FREECAD ASSEMBLY — COMPONENT RECIPES ("wardrobe_corpus02_jan")

This assembly document has 10 components, labeled P0..P9 below (a component is one placed body or linked part). 6 of them carry a construction recipe — the FreeCAD feature program that regenerates the part from scratch, quoted from this document or its linked companion documents; the rest are supplied as boundary geometry only. No exploded tour is included for this assembly.
COMPONENT P0 — geometry summary ("hettich-level-adjustment"; no construction recipe available for this part):
  bounding box: 80.0 x 63.5 x 30.0 mm
  tessellated surface: 3,780 triangles
  volume: 65169 mm^3 (43% of its bounding box)
  symmetry: 2-fold rotationally symmetric about the z axis; mirror-symmetric across its x mid-plane, y mid-plane
COMPONENT P1 — geometry summary ("hettich-level-adjustment001"; no construction recipe available for this part):
  bounding box: 80.0 x 63.5 x 30.0 mm
  tessellated surface: 3,780 triangles
  volume: 65169 mm^3 (43% of its bounding box)
  symmetry: 2-fold rotationally symmetric about the z axis; mirror-symmetric across its x mid-plane, y mid-plane
COMPONENT P2 — geometry summary ("hettich-level-adjustment002"; no construction recipe available for this part):
  bounding box: 80.0 x 63.5 x 30.0 mm
  tessellated surface: 3,780 triangles
  volume: 65169 mm^3 (43% of its bounding box)
  symmetry: 2-fold rotationally symmetric about the z axis; mirror-symmetric across its x mid-plane, y mid-plane
COMPONENT P3 — geometry summary ("hettich-level-adjustment003"; no construction recipe available for this part):
  bounding box: 80.0 x 63.5 x 30.0 mm
  tessellated surface: 3,780 triangles
  volume: 65169 mm^3 (43% of its bounding box)
  symmetry: 2-fold rotationally symmetric about the z axis; mirror-symmetric across its x mid-plane, y mid-plane
COMPONENT P4 — recipe-attached ("wardrobe_backplate_corpus02_jan", a linked part whose construction recipe lives in a companion FreeCAD document of the same project; that document's serialized recipe follows).
Construction recipe (the companion document, serialized — sketch geometry with constraints, then the solid features built on it; lengths are millimeters unless a unit is written):

FCSTD DOCUMENT  (FreeCAD 1.0RUnknown)
Label: wardrobe_backplate_corpus02_jan
License: All rights reserved
LicenseURL: https://en.wikipedia.org/wiki/All_rights_reserved
objects: Sketcher::SketchObject×1, PartDesign::Pad×1, PartDesign::CoordinateSystem×1, PartDesign::Body×1
note: 7 computed .brp shape members not serialized (recipe doc carries the construction recipe); baked Part::Feature solids carry a one-line shape summary decoded from their .brp
EXTERNAL_REF file=../../mastersketch.FCStd obj=Spreadsheet

FEATURE [Sketcher::SketchObject] Sketch004
  ArcFitTolerance = 1e-06
  AttachmentSupport = -> [XZ_Plane006]
  FullyConstrained = true
  MakeInternals = false
  MapMode = 5
  Placement = pos=(0,0,0) rot=(1,0,0;1.5708rad)
  expr: Constraints[10] = mastersketch#Spreadsheet.corpus_width
  expr: Constraints[11] = mastersketch#Spreadsheet.corpus02_height
  sketch-geometry (5):
    g0: LineSegment StartX=-270 StartY=-390 StartZ=0 EndX=270 EndY=-390 EndZ=0
    g1: LineSegment StartX=270 StartY=-390 StartZ=0 EndX=270 EndY=390 EndZ=0
    g2: LineSegment StartX=270 StartY=390 StartZ=0 EndX=-270 EndY=390 EndZ=0
    g3: LineSegment StartX=-270 StartY=390 StartZ=0 EndX=-270 EndY=-390 EndZ=0
    g4: GeomPoint [constr] X=0 Y=0 Z=0
  constraints (12):
    c: Coincident(g0,g1)
    c: Coincident(g1,g2)
    c: Coincident(g2,g3)
    c: Coincident(g3,g0)
    c: Horizontal(g0)
    c: Horizontal(g2)
    c: Vertical(g1)
    c: Vertical(g3)
    c: Symmetric(g2,g0,g4)
    c: Coincident(g4,g-1)
    c: DistanceX(g0,g0) = 540
    c: DistanceY(g3,g3) = 780
FEATURE [PartDesign::Pad] Pad004
  Direction = (0,-1,2e-16)
  Length = 19
  Length2 = 10
  Placement = pos=(0,0,0) rot=(1,0,0;1.5708rad)
  Profile = -> Sketch004
  ReferenceAxis = -> Sketch004 [N_Axis]
  Refine = true
  Suppressed = false
  Type = 0
  expr: Length = mastersketch#Spreadsheet.corpus_backplate_thickness
FEATURE [PartDesign::CoordinateSystem] LCS_1
  AttacherType = Attacher::AttachEngine3D
  AttachmentSupport = -> [Pad004]
  MapMode = 45
  Placement = pos=(0,-19,-390) rot=(0.57735,0.57735,0.57735;2.0944rad)
FEATURE [PartDesign::Body] Body004  label="wardrobe_backplate_corpus02_jan"
  AllowCompound = false
  Group = -> [Sketch004,Pad004,LCS_1]
  Origin = -> Origin006
  Tip = -> Pad004
COMPONENT P5 — recipe-attached ("wardrobe_base_jan", a linked part whose construction recipe lives in a companion FreeCAD document of the same project; that document's serialized recipe follows).
Construction recipe (the companion document, serialized — sketch geometry with constraints, then the solid features built on it; lengths are millimeters unless a unit is written):

FCSTD DOCUMENT  (FreeCAD 1.0RUnknown)
Label: wardrobe_base_jan
License: All rights reserved
LicenseURL: https://en.wikipedia.org/wiki/All_rights_reserved
objects: PartDesign::CoordinateSystem×9, Sketcher::SketchObject×2, PartDesign::Pad×1, PartDesign::Body×1
note: 17 computed .brp shape members not serialized (recipe doc carries the construction recipe); baked Part::Feature solids carry a one-line shape summary decoded from their .brp
EXTERNAL_REF file=../../mastersketch.FCStd obj=Spreadsheet

FEATURE [Sketcher::SketchObject] Sketch
  ArcFitTolerance = 1e-06
  AttachmentSupport = -> [XY_Plane]
  FullyConstrained = true
  MakeInternals = false
  MapMode = 5
  expr: Constraints[10] = mastersketch#Spreadsheet.corpus_width
  expr: Constraints[11] = mastersketch#Spreadsheet.corpus_depth
  sketch-geometry (5):
    g0: LineSegment StartX=-270 StartY=-300 StartZ=0 EndX=270 EndY=-300 EndZ=0
    g1: LineSegment StartX=270 StartY=-300 StartZ=0 EndX=270 EndY=300 EndZ=0
    g2: LineSegment StartX=270 StartY=300 StartZ=0 EndX=-270 EndY=300 EndZ=0
    g3: LineSegment StartX=-270 StartY=300 StartZ=0 EndX=-270 EndY=-300 EndZ=0
    g4: GeomPoint [constr] X=0 Y=0 Z=0
  constraints (12):
    c: Coincident(g0,g1)
    c: Coincident(g1,g2)
    c: Coincident(g2,g3)
    c: Coincident(g3,g0)
    c: Horizontal(g0)
    c: Horizontal(g2)
    c: Vertical(g1)
    c: Vertical(g3)
    c: Symmetric(g2,g0,g4)
    c: Coincident(g4,g-1)
    c: DistanceX(g0,g0) = 540
    c: DistanceY(g3,g3) = 600
FEATURE [PartDesign::Pad] Pad
  Direction = (0,0,1)
  Length = 19
  Length2 = 10
  Profile = -> Sketch
  ReferenceAxis = -> Sketch [N_Axis]
  Refine = true
  Suppressed = false
  Type = 0
  expr: Length = mastersketch#Spreadsheet.corpus_outer_thickness
FEATURE [PartDesign::CoordinateSystem] LCS_1  label="LCS_left"
  AttacherType = Attacher::AttachEngine3D
  AttachmentSupport = -> [Pad]
  MapMode = 45
  Placement = pos=(-270,1.42e-14,19) rot=(0,0.707107,0.707107;3.14159rad)
FEATURE [PartDesign::CoordinateSystem] LCS_right  label="LCS-right"
  AttacherType = Attacher::AttachEngine3D
  AttachmentSupport = -> [Pad]
  MapMode = 45
  Placement = pos=(270,-1.42e-14,19) rot=(0,0.707107,0.707107;3.14159rad)
FEATURE [PartDesign::CoordinateSystem] LCS_center
  AttacherType = Attacher::AttachEngine3D
FEATURE [Sketcher::SketchObject] Sketch_1  label="feet_placement"
  ArcFitTolerance = 1e-06
  AttachmentSupport = -> [Pad]
  FullyConstrained = true
  MakeInternals = false
  MapMode = 5
  Placement = pos=(0,0,0) rot=(1,0,0;3.14159rad)
  expr: Constraints[10] = mastersketch#Spreadsheet.corpus_width - 100
  expr: Constraints[11] = mastersketch#Spreadsheet.corpus_depth - 140
  sketch-geometry (5):
    g0: LineSegment StartX=-220 StartY=-230 StartZ=0 EndX=220 EndY=-230 EndZ=0
    g1: LineSegment StartX=220 StartY=-230 StartZ=0 EndX=220 EndY=230 EndZ=0
    g2: LineSegment StartX=220 StartY=230 StartZ=0 EndX=-220 EndY=230 EndZ=0
    g3: LineSegment StartX=-220 StartY=230 StartZ=0 EndX=-220 EndY=-230 EndZ=0
    g4: GeomPoint [constr] X=0 Y=0 Z=0
  constraints (12):
    c: Coincident(g0,g1)
    c: Coincident(g1,g2)
    c: Coincident(g2,g3)
    c: Coincident(g3,g0)
    c: Horizontal(g0)
    c: Horizontal(g2)
    c: Vertical(g1)
    c: Vertical(g3)
    c: Symmetric(g2,g0,g4)
    c: Coincident(g4,g-1)
    c: DistanceX(g0,g0) = 440
    c: DistanceY(g3,g3) = 460
FEATURE [PartDesign::CoordinateSystem] LCS_2  label="LCS_feet0"
  AttacherType = Attacher::AttachEngine3D
  AttachmentSupport = -> [Sketch_1]
  MapMode = 1
  Placement = pos=(-220,-230,0) rot=(0,0,1;0rad)
FEATURE [PartDesign::CoordinateSystem] LCS_feet1
  AttacherType = Attacher::AttachEngine3D
  AttachmentSupport = -> [Sketch_1]
  MapMode = 1
  Placement = pos=(220,-230,0) rot=(0,0,1;0rad)
FEATURE [PartDesign::CoordinateSystem] LCS_feet2
  AttacherType = Attacher::AttachEngine3D
  AttachmentSupport = -> [Sketch_1]
  MapMode = 1
  Placement = pos=(220,230,0) rot=(0,0,1;0rad)
FEATURE [PartDesign::CoordinateSystem] LCS_feet3
  AttacherType = Attacher::AttachEngine3D
  AttachmentSupport = -> [Sketch_1]
  MapMode = 1
  Placement = pos=(-220,230,0) rot=(0,0,1;0rad)
FEATURE [PartDesign::CoordinateSystem] LCS_back
  AttacherType = Attacher::AttachEngine3D
  AttachmentSupport = -> [Pad]
  MapMode = 45
  Placement = pos=(0,300,0) rot=(0.57735,0.57735,0.57735;2.0944rad)
FEATURE [PartDesign::CoordinateSystem] LCS_door
  AttacherType = Attacher::AttachEngine3D
  AttachmentSupport = -> [Pad]
  MapMode = 7
  Placement = pos=(270,-300,0) rot=(0,1,0;3.14159rad)
FEATURE [PartDesign::Body] Body  label="wardrobe_base_jan"
  AllowCompound = false
  Group = -> [Sketch,Pad,LCS_1,LCS_right,LCS_center,Sketch_1,LCS_2,LCS_feet1,LCS_feet2,LCS_feet3,LCS_back,LCS_door]
  Origin = -> Origin
  Tip = -> Pad
COMPONENT P6 — recipe-attached ("wardrobe_door_corpus02_jan", a linked part whose construction recipe lives in a companion FreeCAD document of the same project; that document's serialized recipe follows).
Construction recipe (the companion document, serialized — sketch geometry with constraints, then the solid features built on it; lengths are millimeters unless a unit is written):

FCSTD DOCUMENT  (FreeCAD 1.0R39285 (Git))
Label: wardrobe_door_corpus02_jan
License: All rights reserved
LicenseURL: https://en.wikipedia.org/wiki/All_rights_reserved
objects: TechDraw::DrawViewDimension×5, PartDesign::CoordinateSystem×2, TechDraw::DrawProjGroupItem×2, Sketcher::SketchObject×1, PartDesign::Pad×1, PartDesign::Body×1, TechDraw::DrawSVGTemplate×1, TechDraw::DrawViewAnnotation×1, TechDraw::DrawPage×1, App::Part×1
note: 15 computed .brp shape members not serialized (recipe doc carries the construction recipe); baked Part::Feature solids carry a one-line shape summary decoded from their .brp
EXTERNAL_REF file=../../mastersheet.FCStd obj=Spreadsheet
EXTERNAL_REF file=../../mastersketch.FCStd obj=Sketch

FEATURE [Sketcher::SketchObject] Sketch
  ArcFitTolerance = 1e-06
  AttachmentSupport = -> [XY_Plane]
  FullyConstrained = true
  MakeInternals = false
  MapMode = 5
  expr: Constraints[0] = mastersketch#Sketch.Constraints.corpus02_door_height
  expr: Constraints[10] = mastersketch#Sketch.Constraints.alpha
  expr: Constraints[3] = mastersheet#Spreadsheet.corpus_width - 5
  sketch-geometry (4):
    g0: LineSegment StartX=0 StartY=0 StartZ=0 EndX=0 EndY=1413.69 EndZ=0
    g1: LineSegment StartX=0 StartY=0 StartZ=0 EndX=-535 EndY=0 EndZ=0
    g2: LineSegment StartX=-535 StartY=0 StartZ=0 EndX=-535 EndY=787.688 EndZ=0
    g3: LineSegment StartX=-535 StartY=787.688 StartZ=0 EndX=0 EndY=1413.69 EndZ=0
  constraints (11):
    c: Distance(g0) = 1413.69
    c: Coincident(g0,g-1)
    c: Vertical(g0)
    c: Distance(g1) = 535
    c: Coincident(g1,g0)
    c: PointOnObject(g1,g-1)
    c: Vertical(g2)
    c: Coincident(g3,g2)
    c: Coincident(g2,g1)
    c: Coincident(g3,g0)
    c: Angle(g2,g3) = 2.43442
FEATURE [PartDesign::Pad] Pad
  Direction = (0,0,1)
  Length = 19
  Length2 = 10
  Profile = -> Sketch
  ReferenceAxis = -> Sketch [N_Axis]
  Refine = true
  Suppressed = false
  Type = 0
FEATURE [PartDesign::Body] Body  label="wardrobe_door_corpus02_jan"
  AllowCompound = false
  Group = -> [Sketch,Pad]
  Origin = -> Origin
  Tip = -> Pad
FEATURE [PartDesign::CoordinateSystem] LCS_1
  AttacherType = Attacher::AttachEngine3D
  AttachmentSupport = -> [Pad]
  MapMode = 7
  Placement = pos=(0,0,0) rot=(1,0,0;1.5708rad)
FEATURE [TechDraw::DrawSVGTemplate] Template  label="Vorlage"
  Height = 210
  Orientation = 1
  Template = <userpath>/scoop/apps/freecad/current/data/Mod/TechDraw/Templates/A4_Landscape_TD.svg
  Width = 297
FEATURE [TechDraw::DrawProjGroupItem] View
  CoarseView = false
  Direction = (0,1e-16,-1)
  Focus = 100
  HardHidden = false
  IsoCount = 0
  IsoHidden = false
  IsoVisible = false
  LockPosition = false
  Perspective = false
  Rotation = 0
  RotationVector = (1,0,0)
  Scale = 0.1
  ScaleType = 2
  ScrubCount = 1
  SeamHidden = false
  SeamVisible = false
  SmoothHidden = false
  SmoothVisible = true
  Source = -> [Body]
  Type = 0
  X = 139.755
  XDirection = (-1e-16,-1,-1e-16)
  Y = 148.199
FEATURE [TechDraw::DrawProjGroupItem] View001
  CoarseView = false
  Direction = (-1,-1e-16,0)
  Focus = 100
  HardHidden = false
  IsoCount = 0
  IsoHidden = false
  IsoVisible = false
  LockPosition = false
  Perspective = false
  Rotation = 0
  RotationVector = (1,0,0)
  Scale = 0.1
  ScaleType = 2
  ScrubCount = 1
  SeamHidden = false
  SeamVisible = false
  SmoothHidden = false
  SmoothVisible = true
  Source = -> [Body]
  Type = 0
  X = 139.755
  XDirection = (1e-16,-1,0)
  Y = 90.1338
FEATURE [TechDraw::DrawViewDimension] Dimension  label="Maß"
  AngleOverride = false
  Arbitrary = false
  ArbitraryTolerances = false
  BoxCorners = (2) [(-70.6847,-26.75,0),(70.6847,26.75,0)]
  EqualTolerance = true
  ExtensionAngle = 0
  FormatSpec = %.1w
  FormatSpecOverTolerance = %+.1w
  FormatSpecUnderTolerance = %+.1w
  Inverted = false
  LineAngle = 0
  LockPosition = false
  MeasureType = 1
  OverTolerance = 0
  References2D = -> [View]
  Rotation = 0
  ScaleType = 0
  TheoreticalExact = false
  Type = 1
  UnderTolerance = 0
  X = 0
  Y = -33.1734
FEATURE [TechDraw::DrawViewDimension] Dimension001  label="Maß001"
  AngleOverride = false
  Arbitrary = false
  ArbitraryTolerances = false
  BoxCorners = (2) [(-70.6847,-26.75,0),(70.6847,26.75,0)]
  EqualTolerance = true
  ExtensionAngle = 0
  FormatSpec = %.1w
  FormatSpecOverTolerance = %+.1w
  FormatSpecUnderTolerance = %+.1w
  Inverted = false
  LineAngle = 0
  LockPosition = false
  MeasureType = 1
  OverTolerance = 0
  References2D = -> [View]
  Rotation = 0
  ScaleType = 0
  TheoreticalExact = false
  Type = 2
  UnderTolerance = 0
  X = 76.0797
  Y = 0
FEATURE [TechDraw::DrawViewDimension] Dimension002  label="Maß002"
  AngleOverride = false
  Arbitrary = false
  ArbitraryTolerances = false
  BoxCorners = (2) [(-70.6847,-26.75,0),(70.6847,26.75,0)]
  EqualTolerance = true
  ExtensionAngle = 0
  FormatSpec = %.1w
  FormatSpecOverTolerance = %+.1w
  FormatSpecUnderTolerance = %+.1w
  Inverted = false
  LineAngle = 0
  LockPosition = false
  MeasureType = 1
  OverTolerance = 0
  References2D = -> [View]
  Rotation = 0
  ScaleType = 0
  TheoreticalExact = false
  Type = 1
  UnderTolerance = 0
  X = 31.3003
  Y = 43.1168
FEATURE [TechDraw::DrawViewDimension] Dimension003  label="Maß003"
  AngleOverride = false
  Arbitrary = false
  ArbitraryTolerances = false
  BoxCorners = (2) [(-70.6847,-0.95,0),(70.6847,0.95,0)]
  EqualTolerance = true
  ExtensionAngle = 0
  FormatSpec = %.1w
  FormatSpecOverTolerance = %+.1w
  FormatSpecUnderTolerance = %+.1w
  Inverted = false
  LineAngle = 0
  LockPosition = false
  MeasureType = 1
  OverTolerance = 0
  References2D = -> [View001]
  Rotation = 0
  ScaleType = 0
  TheoreticalExact = false
  Type = 0
  UnderTolerance = 0
  X = 76.6584
  Y = -13.0761
FEATURE [TechDraw::DrawViewDimension] Dimension004  label="Maß004"
  AngleOverride = false
  Arbitrary = false
  ArbitraryTolerances = false
  BoxCorners = (2) [(-70.6847,-26.75,0),(70.6847,26.75,0)]
  EqualTolerance = true
  ExtensionAngle = 0
  FormatSpec = (%.1w)
  FormatSpecOverTolerance = %+.1w
  FormatSpecUnderTolerance = %+.1w
  Inverted = false
  LineAngle = 0
  LockPosition = false
  MeasureType = 1
  OverTolerance = 0
  References2D = -> [View]
  Rotation = 0
  ScaleType = 0
  TheoreticalExact = false
  Type = 6
  UnderTolerance = 0
  X = -0.468348
  Y = 10.2378
FEATURE [TechDraw::DrawViewAnnotation] Annotation  label="Beschriftung"
  Font = MS Shell Dlg 2
  LineSpace = 100
  LockPosition = false
  MaxWidth = -1
  Rotation = 0
  ScaleType = 0
  Text = Artikelnummer: 12391882 oder 6754673
  TextSize = 5
  TextStyle = 0
  X = 208.828
  Y = 61.9887
FEATURE [TechDraw::DrawPage] Page  label="Seite"
  KeepUpdated = true
  NextBalloonIndex = 1
  ProjectionType = 0
  Template = -> Template
  Views = -> [View,View001,Dimension,Dimension001,Dimension002,Dimension003,Dimension004,Annotation]
FEATURE [PartDesign::CoordinateSystem] LCS_Origin
  AttacherType = Attacher::AttachEngine3D
  AttachmentSupport = -> [X_Axis001]
  MapMode = 2
FEATURE [App::Part] wardrobe_door_corpus02_jan  label="wardrobe_door_corpus02_jan001"
  DrawingName = wardrobe_door_corpus02_jan.FCStd
  Group = -> [LCS_Origin,LCS_1,Body]
  Origin = -> Origin001
  PartDescription = wardrobe_door_corpus02_jan
  PartID = wardrobe_door_corpus02_jan
COMPONENT P7 — recipe-attached ("wardrobe_left_corpus02_jan", a linked part whose construction recipe lives in a companion FreeCAD document of the same project; that document's serialized recipe follows).
Construction recipe (the companion document, serialized — sketch geometry with constraints, then the solid features built on it; lengths are millimeters unless a unit is written):

FCSTD DOCUMENT  (FreeCAD 1.0RUnknown)
Label: wardrobe_left_corpus02_jan
License: All rights reserved
LicenseURL: https://en.wikipedia.org/wiki/All_rights_reserved
objects: PartDesign::CoordinateSystem×3, Sketcher::SketchObject×1, PartDesign::Pad×1, PartDesign::Body×1
note: 9 computed .brp shape members not serialized (recipe doc carries the construction recipe); baked Part::Feature solids carry a one-line shape summary decoded from their .brp
EXTERNAL_REF file=../../mastersketch.FCStd obj=Spreadsheet

FEATURE [Sketcher::SketchObject] Sketch001
  ArcFitTolerance = 1e-06
  AttachmentSupport = -> [YZ_Plane001]
  FullyConstrained = true
  MakeInternals = false
  MapMode = 5
  Placement = pos=(0,0,0) rot=(0.57735,0.57735,0.57735;2.0944rad)
  expr: Constraints[10] = mastersketch#Spreadsheet.corpus_depth
  expr: Constraints[11] = mastersketch#Spreadsheet.corpus02_height - 2 * mastersketch#Spreadsheet.corpus_outer_thickness
  sketch-geometry (5):
    g0: LineSegment StartX=-300 StartY=-371 StartZ=0 EndX=300 EndY=-371 EndZ=0
    g1: LineSegment StartX=300 StartY=-371 StartZ=0 EndX=300 EndY=371 EndZ=0
    g2: LineSegment StartX=300 StartY=371 StartZ=0 EndX=-300 EndY=371 EndZ=0
    g3: LineSegment StartX=-300 StartY=371 StartZ=0 EndX=-300 EndY=-371 EndZ=0
    g4: GeomPoint [constr] X=0 Y=0 Z=0
  constraints (12):
    c: Coincident(g0,g1)
    c: Coincident(g1,g2)
    c: Coincident(g2,g3)
    c: Coincident(g3,g0)
    c: Horizontal(g0)
    c: Horizontal(g2)
    c: Vertical(g1)
    c: Vertical(g3)
    c: Symmetric(g2,g0,g4)
    c: Coincident(g4,g-1)
    c: DistanceX(g0,g0) = 600
    c: DistanceY(g3,g3) = 742
FEATURE [PartDesign::Pad] Pad001
  Direction = (1,0,0)
  Length = 19
  Length2 = 10
  Placement = pos=(0,0,0) rot=(1,1,1;2.0944rad)
  Profile = -> Sketch001
  ReferenceAxis = -> Sketch001 [N_Axis]
  Refine = true
  Suppressed = false
  Type = 0
  expr: Length = mastersketch#Spreadsheet.corpus_outer_thickness
FEATURE [PartDesign::CoordinateSystem] LCS_1  label="LCS_bottom"
  AttacherType = Attacher::AttachEngine3D
  AttachmentSupport = -> [Pad001]
  MapMode = 45
  Placement = pos=(0,-1.42e-14,-371) rot=(0,0.707107,0.707107;3.14159rad)
FEATURE [PartDesign::CoordinateSystem] LCS_top
  AttacherType = Attacher::AttachEngine3D
  AttachmentSupport = -> [Pad001]
  MapMode = 45
  Placement = pos=(0,1.42e-14,371) rot=(0,0.707107,0.707107;3.14159rad)
FEATURE [PartDesign::CoordinateSystem] LCS_inner
  AttacherType = Attacher::AttachEngine3D
  AttachmentSupport = -> [Pad001]
  MapMode = 45
  Placement = pos=(19,-1.82e-14,-371) rot=(0,0.707107,0.707107;3.14159rad)
FEATURE [PartDesign::Body] Body001  label="wardrobe_left_corpus02_jan"
  AllowCompound = false
  Group = -> [Sketch001,Pad001,LCS_1,LCS_top,LCS_inner]
  Origin = -> Origin001
  Tip = -> Pad001
COMPONENT P8 — recipe-attached ("wardrobe_right_corpus02_jan", a linked part whose construction recipe lives in a companion FreeCAD document of the same project; that document's serialized recipe follows).
Construction recipe (the companion document, serialized — sketch geometry with constraints, then the solid features built on it; lengths are millimeters unless a unit is written):

FCSTD DOCUMENT  (FreeCAD 1.0RUnknown)
Label: wardrobe_right_corpus02_jan
License: All rights reserved
LicenseURL: https://en.wikipedia.org/wiki/All_rights_reserved
objects: Sketcher::SketchObject×1, PartDesign::Pad×1, PartDesign::CoordinateSystem×1, PartDesign::Body×1
note: 7 computed .brp shape members not serialized (recipe doc carries the construction recipe); baked Part::Feature solids carry a one-line shape summary decoded from their .brp
EXTERNAL_REF file=../../mastersketch.FCStd obj=Spreadsheet

FEATURE [Sketcher::SketchObject] Sketch002
  ArcFitTolerance = 1e-06
  AttachmentSupport = -> [YZ_Plane004]
  FullyConstrained = true
  MakeInternals = false
  MapMode = 5
  Placement = pos=(0,0,0) rot=(0.57735,0.57735,0.57735;2.0944rad)
  expr: Constraints[10] = mastersketch#Spreadsheet.corpus_depth
  expr: Constraints[11] = mastersketch#Spreadsheet.corpus02_height - 2 * mastersketch#Spreadsheet.corpus_outer_thickness
  sketch-geometry (5):
    g0: LineSegment StartX=-300 StartY=-371 StartZ=0 EndX=300 EndY=-371 EndZ=0
    g1: LineSegment StartX=300 StartY=-371 StartZ=0 EndX=300 EndY=371 EndZ=0
    g2: LineSegment StartX=300 StartY=371 StartZ=0 EndX=-300 EndY=371 EndZ=0
    g3: LineSegment StartX=-300 StartY=371 StartZ=0 EndX=-300 EndY=-371 EndZ=0
    g4: GeomPoint [constr] X=0 Y=0 Z=0
  constraints (12):
    c: Coincident(g0,g1)
    c: Coincident(g1,g2)
    c: Coincident(g2,g3)
    c: Coincident(g3,g0)
    c: Horizontal(g0)
    c: Horizontal(g2)
    c: Vertical(g1)
    c: Vertical(g3)
    c: Symmetric(g2,g0,g4)
    c: Coincident(g4,g-1)
    c: DistanceX(g0,g0) = 600
    c: DistanceY(g3,g3) = 742
FEATURE [PartDesign::Pad] Pad002
  Direction = (1,0,0)
  Length = 19
  Length2 = 10
  Placement = pos=(0,0,0) rot=(1,1,1;2.0944rad)
  Profile = -> Sketch002
  ReferenceAxis = -> Sketch002 [N_Axis]
  Refine = true
  Suppressed = false
  Type = 0
  expr: Length = mastersketch#Spreadsheet.corpus_outer_thickness
FEATURE [PartDesign::CoordinateSystem] LCS_1
  AttacherType = Attacher::AttachEngine3D
  AttachmentSupport = -> [Pad002]
  MapMode = 45
  Placement = pos=(19,-1.82e-14,-371) rot=(0,0.707107,0.707107;3.14159rad)
FEATURE [PartDesign::Body] Body002  label="wardrobe_right_corpus02_jan"
  AllowCompound = false
  Group = -> [Sketch002,Pad002,LCS_1]
  Origin = -> Origin004
  Tip = -> Pad002
COMPONENT P9 — recipe-attached ("wardrobe_top_jan", a linked part whose construction recipe lives in a companion FreeCAD document of the same project; that document's serialized recipe follows).
Construction recipe (the companion document, serialized — sketch geometry with constraints, then the solid features built on it; lengths are millimeters unless a unit is written):

FCSTD DOCUMENT  (FreeCAD 1.0RUnknown)
Label: wardrobe_top_jan
License: All rights reserved
LicenseURL: https://en.wikipedia.org/wiki/All_rights_reserved
objects: Sketcher::SketchObject×1, PartDesign::Pad×1, PartDesign::CoordinateSystem×1, PartDesign::Body×1
note: 7 computed .brp shape members not serialized (recipe doc carries the construction recipe); baked Part::Feature solids carry a one-line shape summary decoded from their .brp
EXTERNAL_REF file=../../mastersketch.FCStd obj=Spreadsheet

FEATURE [Sketcher::SketchObject] Sketch003
  ArcFitTolerance = 1e-06
  AttachmentSupport = -> [XY_Plane005]
  FullyConstrained = true
  MakeInternals = false
  MapMode = 5
  expr: Constraints[10] = mastersketch#Spreadsheet.corpus_width
  expr: Constraints[11] = mastersketch#Spreadsheet.corpus_depth
  sketch-geometry (5):
    g0: LineSegment StartX=-270 StartY=-300 StartZ=0 EndX=270 EndY=-300 EndZ=0
    g1: LineSegment StartX=270 StartY=-300 StartZ=0 EndX=270 EndY=300 EndZ=0
    g2: LineSegment StartX=270 StartY=300 StartZ=0 EndX=-270 EndY=300 EndZ=0
    g3: LineSegment StartX=-270 StartY=300 StartZ=0 EndX=-270 EndY=-300 EndZ=0
    g4: GeomPoint [constr] X=0 Y=0 Z=0
  constraints (12):
    c: Coincident(g0,g1)
    c: Coincident(g1,g2)
    c: Coincident(g2,g3)
    c: Coincident(g3,g0)
    c: Horizontal(g0)
    c: Horizontal(g2)
    c: Vertical(g1)
    c: Vertical(g3)
    c: Symmetric(g2,g0,g4)
    c: Coincident(g4,g-1)
    c: DistanceX(g0,g0) = 540
    c: DistanceY(g3,g3) = 600
FEATURE [PartDesign::Pad] Pad003
  Direction = (0,0,1)
  Length = 19
  Length2 = 10
  Profile = -> Sketch003
  ReferenceAxis = -> Sketch003 [N_Axis]
  Refine = true
  Suppressed = false
  Type = 0
  expr: Length = mastersketch#Spreadsheet.corpus_outer_thickness
FEATURE [PartDesign::CoordinateSystem] LCS_left
  AttacherType = Attacher::AttachEngine3D
  AttachmentSupport = -> [Pad003]
  MapMode = 45
  Placement = pos=(-270,1.42e-14,0) rot=(0,0.707107,0.707107;3.14159rad)
FEATURE [PartDesign::Body] Body003  label="wardrobe_top_jan"
  AllowCompound = false
  Group = -> [Sketch003,Pad003,LCS_left]
  Origin = -> Origin005
  Tip = -> Pad003
PROVENANCE & LICENSES
A FreeCAD (.FCStd) document from a public repository crawl; recipes are the document's own serialized feature recipes (and, for linked parts, companion documents' recipes).
License: as declared in the source repository (recorded in the dataset sidecar).
